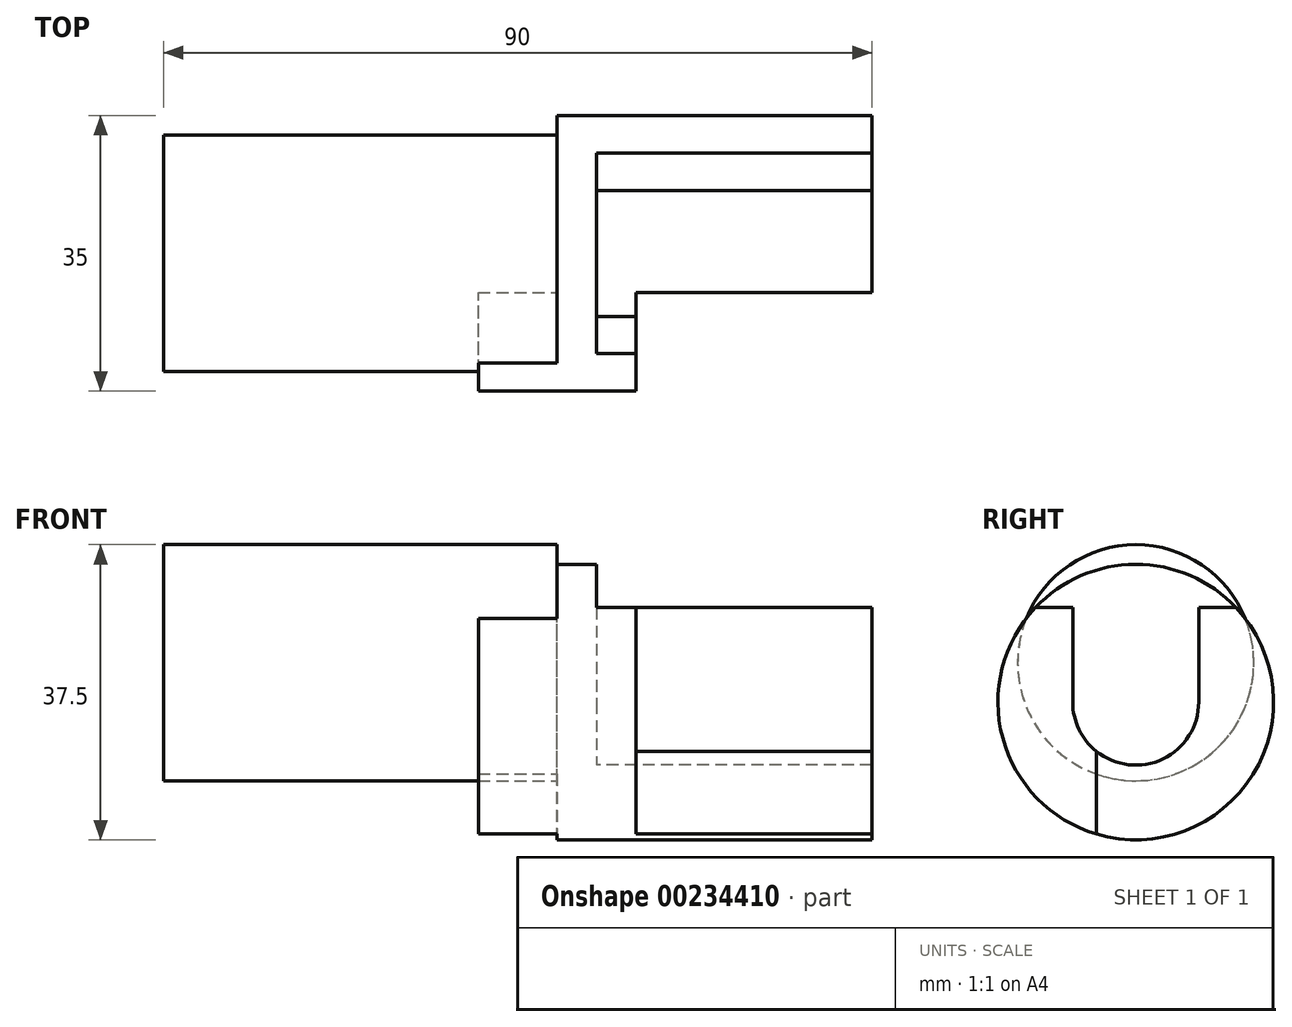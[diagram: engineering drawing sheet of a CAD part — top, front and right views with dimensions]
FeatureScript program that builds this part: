
annotation { "Feature Type Name" : "Feature", "Feature Type Description" : "" }
export const myFeature = defineFeature(function(context is Context, id is Id, definition is map)
    precondition{}
    {
        {
            var Q0;
            Q0=qCreatedBy(makeId("Right.planeOp"),FACE);
            var sketch = newSketch(context, id + "F0", { "sketchPlane" : qUnion([Q0])});
            skCircle(sketch, "E0", {"center": v(0, 0) * mm, "radius": 17.5 * mm});
            skLineSegment(sketch, "E1", {"start": v(-5, -6.24) * mm, "end": v(-5, -16.77) * mm});
            skLineSegment(sketch, "E2", {"start": v(8, 12) * mm, "end": v(12.74, 12) * mm});
            skLineSegment(sketch, "E3", {"start": v(8, 12) * mm, "end": v(8, 0) * mm});
            skArc(sketch, "E4", {"start": v(-8, 0) * mm, "mid": v(0, -8) * mm, "end": v(8, 0) * mm});
            skPoint(sketch, "E5", {"position": v(-8, 0) * mm});
            skLineSegment(sketch, "E6", {"start": v(-12.74, 12) * mm, "end": v(-8, 12) * mm});
            skLineSegment(sketch, "E7", {"start": v(-8, 12) * mm, "end": v(-8, 0) * mm});
            skCircle(sketch, "E8", {"center": v(0, 5) * mm, "radius": 15 * mm});
            skPoint(sketch, "E9", {"position": v(0, -17.5) * mm});
            skPoint(sketch, "E10", {"position": v(17.5, 0) * mm});
            skPoint(sketch, "E11", {"position": v(-5, -16.77) * mm});
            skSolve(sketch);
        }
        {
            var Q0;
            {var subQ0=sQuery(id+"F0.wireOp",EDGE,"E1");var subQ1=sQuery(id+"F0.wireOp",EDGE,"E0");var subQ2=makeQuery(id+"F0.imprint","INTERSECT",VERTEX,{"derivedFrom":[subQ1,subQ0]});Q0=makeQuery(id+"F0.imprint","IMPRINT",FACE,{"disambiguationData":[TD([[makeQuery(id+"F0.imprint","IMPRINT",EDGE,{"disambiguationData":[TD([[subQ2,-1.0]])],"derivedFrom":subQ1}),1.0]])]});}
            var Q1;
            {var subQ1=sQuery(id+"F0.wireOp",EDGE,"E2");Q1=makeQuery(id+"F0.imprint","IMPRINT",FACE,{"disambiguationData":[TD([[makeQuery(id+"F0.imprint","IMPRINT",EDGE,{"derivedFrom":subQ1}),-1.0]])]});}
            var Q2;
            {var subQ4=sQuery(id+"F0.wireOp",EDGE,"E2");Q2=makeQuery(id+"F0.imprint","IMPRINT",FACE,{"disambiguationData":[TD([[makeQuery(id+"F0.imprint","IMPRINT",EDGE,{"derivedFrom":subQ4}),1.0]])]});}
            var Q3;
            {var subQ0=sQuery(id+"F0.wireOp",EDGE,"E6");Q3=makeQuery(id+"F0.imprint","IMPRINT",FACE,{"disambiguationData":[TD([[makeQuery(id+"F0.imprint","IMPRINT",EDGE,{"derivedFrom":subQ0}),-1.0]])]});}
            var Q4;
            {var subQ0=sQuery(id+"F0.wireOp",EDGE,"E1");var subQ1=sQuery(id+"F0.wireOp",EDGE,"E0");var subQ2=makeQuery(id+"F0.imprint","INTERSECT",VERTEX,{"derivedFrom":[subQ1,subQ0]});Q4=makeQuery(id+"F0.imprint","IMPRINT",FACE,{"disambiguationData":[TD([[makeQuery(id+"F0.imprint","IMPRINT",EDGE,{"disambiguationData":[TD([[subQ2,1.0]])],"derivedFrom":subQ1}),1.0]])]});}
            extrude(context, id + "F1", {"entities" : qUnion([Q0, Q1, Q2, Q3, Q4]), "depth" : 5 * mm});
        }
        {
            var Q0;
            Q0=makeQuery(id+"F1.opExtrude","CAP_FACE",FACE,{"disambiguationData":[OSD([sQuery(id+"F0.wireOp",EDGE,"E0")])],"isStart":false});
            var sketch = newSketch(context, id + "F2", { "sketchPlane" : qUnion([Q0])});
            skLineSegment(sketch, "E12.0", {"start": v(-5, -6.24) * mm, "end": v(-5, -16.77) * mm});
            skCircle(sketch, "E13.0", {"center": v(0, 5) * mm, "radius": 15 * mm});
            skCircle(sketch, "E14.0.0", {"center": v(0, 0) * mm, "radius": 17.5 * mm, "construction": true});
            skCircle(sketch, "E15.0.0", {"center": v(0, 0) * mm, "radius": 17.5 * mm});
            skLineSegment(sketch, "E16.0", {"start": v(8, 12) * mm, "end": v(8, 0) * mm});
            skLineSegment(sketch, "E17.0", {"start": v(8, 12) * mm, "end": v(12.74, 12) * mm});
            skArc(sketch, "E18.0", {"start": v(-8, 0) * mm, "mid": v(0, -8) * mm, "end": v(8, 0) * mm});
            skLineSegment(sketch, "E19.0", {"start": v(-8, 12) * mm, "end": v(-8, 0) * mm});
            skLineSegment(sketch, "E20.0", {"start": v(-12.74, 12) * mm, "end": v(-8, 12) * mm});
            skSolve(sketch);
        }
        {
            var Q0;
            {var subQ0=sQuery(id+"F2.wireOp",EDGE,"E15.0.0");var subQ1=sQuery(id+"F2.wireOp",EDGE,"E12.0");var subQ2=makeQuery(id+"F2.imprint","INTERSECT",VERTEX,{"derivedFrom":[subQ1,subQ0]});Q0=makeQuery(id+"F2.imprint","IMPRINT",FACE,{"disambiguationData":[TD([[makeQuery(id+"F2.imprint","IMPRINT",EDGE,{"disambiguationData":[TD([[subQ2,1.0]])],"derivedFrom":subQ1}),1.0]])]});}
            var Q1;
            {var subQ1=sQuery(id+"F2.wireOp",EDGE,"E16.0");Q1=makeQuery(id+"F2.imprint","IMPRINT",FACE,{"disambiguationData":[TD([[makeQuery(id+"F2.imprint","IMPRINT",EDGE,{"derivedFrom":subQ1}),1.0]])]});}
            extrude(context, id + "F3", {"entities" : qUnion([Q0, Q1]), "operationType" : NewBodyOperationType.ADD, "depth" : 35 * mm});
        }
        {
            var Q0;
            Q0=makeQuery(id+"F1.opExtrude","CAP_FACE",FACE,{"disambiguationData":[OSD([sQuery(id+"F0.wireOp",EDGE,"E0")])],"isStart":false});
            var sketch = newSketch(context, id + "F4", { "sketchPlane" : qUnion([Q0])});
            skLineSegment(sketch, "E21.0.0", {"start": v(-5, -16.77) * mm, "end": v(-5, -6.24) * mm});
            skArc(sketch, "E21.0.1", {"start": v(-5, -6.24) * mm, "mid": v(3.46, -7.21) * mm, "end": v(8, 0) * mm});
            skLineSegment(sketch, "E21.0.2", {"start": v(8, 0) * mm, "end": v(8, 12) * mm});
            skLineSegment(sketch, "E21.0.3", {"start": v(8, 12) * mm, "end": v(12.74, 12) * mm});
            skArc(sketch, "E21.0.4", {"start": v(12.74, 12) * mm, "mid": v(-14.9, 9.18) * mm, "end": v(-5, -16.77) * mm});
            skLineSegment(sketch, "E22.0", {"start": v(-12.74, 12) * mm, "end": v(-8, 12) * mm});
            skLineSegment(sketch, "E23.0", {"start": v(-8, 12) * mm, "end": v(-8, 0) * mm});
            skArc(sketch, "E24.0", {"start": v(-8, 0) * mm, "mid": v(0, -8) * mm, "end": v(8, 0) * mm});
            skCircle(sketch, "E25.0", {"center": v(0, 5) * mm, "radius": 15 * mm});
            skSolve(sketch);
        }
        {
            var Q0;
            {var subQ0=sQuery(id+"F4.wireOp",EDGE,"E21.0.4");var subQ1=sQuery(id+"F4.wireOp",EDGE,"E21.0.0");var subQ2=makeQuery(id+"F4.imprint","INTERSECT",VERTEX,{"derivedFrom":[subQ1,subQ0]});Q0=makeQuery(id+"F4.imprint","IMPRINT",FACE,{"disambiguationData":[TD([[makeQuery(id+"F4.imprint","IMPRINT",EDGE,{"disambiguationData":[TD([[subQ2,1.0]])],"derivedFrom":subQ1}),-1.0]])]});}
            var Q1;
            {var subQ1=sQuery(id+"F4.wireOp",EDGE,"E22.0");Q1=makeQuery(id+"F4.imprint","IMPRINT",FACE,{"disambiguationData":[TD([[makeQuery(id+"F4.imprint","IMPRINT",EDGE,{"derivedFrom":subQ1}),-1.0]])]});}
            extrude(context, id + "F5", {"entities" : qUnion([Q0, Q1]), "operationType" : NewBodyOperationType.ADD, "depth" : 5 * mm});
        }
        {
            var Q0;
            {var subQ0=sQuery(id+"F0.wireOp",EDGE,"E1");var subQ1=sQuery(id+"F0.wireOp",EDGE,"E0");var subQ2=makeQuery(id+"F0.imprint","INTERSECT",VERTEX,{"derivedFrom":[subQ1,subQ0]});Q0=makeQuery(id+"F0.imprint","IMPRINT",FACE,{"disambiguationData":[TD([[makeQuery(id+"F0.imprint","IMPRINT",EDGE,{"disambiguationData":[TD([[subQ2,1.0]])],"derivedFrom":subQ1}),1.0]])]});}
            extrude(context, id + "F6", {"entities" : qUnion([Q0]), "operationType" : NewBodyOperationType.ADD, "oppositeDirection" : true, "depth" : 10 * mm});
        }
        {
            var Q0;
            {var subQ0=sQuery(id+"F0.wireOp",EDGE,"E0");var subQ1=makeQuery(id+"F0.imprint","INTERSECT",VERTEX,{"derivedFrom":[subQ0,sQuery(id+"F0.wireOp",EDGE,"E2")]});Q0=makeQuery(id+"F0.imprint","IMPRINT",FACE,{"disambiguationData":[TD([[makeQuery(id+"F0.imprint","IMPRINT",EDGE,{"disambiguationData":[TD([[subQ1,1.0]])],"derivedFrom":subQ0}),-1.0]])]});}
            var Q1;
            {var subQ4=sQuery(id+"F0.wireOp",EDGE,"E2");Q1=makeQuery(id+"F0.imprint","IMPRINT",FACE,{"disambiguationData":[TD([[makeQuery(id+"F0.imprint","IMPRINT",EDGE,{"derivedFrom":subQ4}),1.0]])]});}
            var Q2;
            {var subQ0=sQuery(id+"F0.wireOp",EDGE,"E6");Q2=makeQuery(id+"F0.imprint","IMPRINT",FACE,{"disambiguationData":[TD([[makeQuery(id+"F0.imprint","IMPRINT",EDGE,{"derivedFrom":subQ0}),-1.0]])]});}
            var Q3;
            {var subQ1=sQuery(id+"F0.wireOp",EDGE,"E2");Q3=makeQuery(id+"F0.imprint","IMPRINT",FACE,{"disambiguationData":[TD([[makeQuery(id+"F0.imprint","IMPRINT",EDGE,{"derivedFrom":subQ1}),-1.0]])]});}
            extrude(context, id + "F7", {"entities" : qUnion([Q0, Q1, Q2, Q3]), "operationType" : NewBodyOperationType.ADD, "oppositeDirection" : true, "depth" : 50 * mm});
        }
    });
